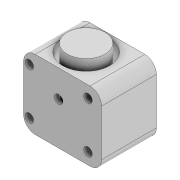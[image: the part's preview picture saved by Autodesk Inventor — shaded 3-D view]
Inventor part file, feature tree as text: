
AUTODESK INVENTOR PART (.ipt)
format: ipt  version: 2022 (Build 260153000, 153)  size: 188,928 bytes
history: native  units: mm
features: extrude x6, sketch x6, projected_geometry x5, fillet x1
ambient origin geometry x8: Origin, YZ Plane, XZ Plane, XY Plane, X Axis, Y Axis, Z Axis, Center Point
bodies: Solid1 (feature_tree)
feature tree (18):
  extrude  "Extrusion1"  Depth=12.2mm
  extrude  "Extrusion2"  Depth=15.0mm TaperAngle=0.0deg
  extrude  "Extrusion3"  Depth=3.0mm
  extrude  "Extrusion8"  Depth=3.0mm
  extrude  "Extrusion9"  Depth=3.0mm
  fillet  "Fillet8"  Radius=2.2mm
  extrude  "Extrusion10"  Depth=3.0mm
  sketch  "Sketch1"  dims[d0=9.8mm d1=12.2mm]
  sketch  "Sketch2"  dims[d3=15.0mm d4=0.0mm d5=2.0mm d6=0.0mm]
  projected_geometry  "Projected Loop1"
  sketch  "Sketch3"  dims[d7=3.0mm d8=0.0mm d36=1.0mm]
  projected_geometry  "Projected Loop2"
  projected_geometry  "Projected Loop6"
  sketch  "Sketch8"  dims[d37=1.0mm d38=3.0mm]
  projected_geometry  "Projected Loop7"
  sketch  "Sketch9"  dims[d39=3.0mm d40=2.2mm d41=2.2mm]
  projected_geometry  "Projected Loop8"
  sketch  "Sketch10"  dims[d42=2.2mm d43=2.2mm d44=3.0mm d45=3.0mm d46=1.5mm d47=1.5mm d48=1.5mm d49=1.5mm d50=3.0mm d51=0.0mm d52=0.0mm d53=3.0mm d54=100.0mm d55=0.0mm d56=2.0mm d57=0.0mm d58=3.0mm d59=2.2mm d60=8.0mm d61=100.0mm d62=0.0mm]
